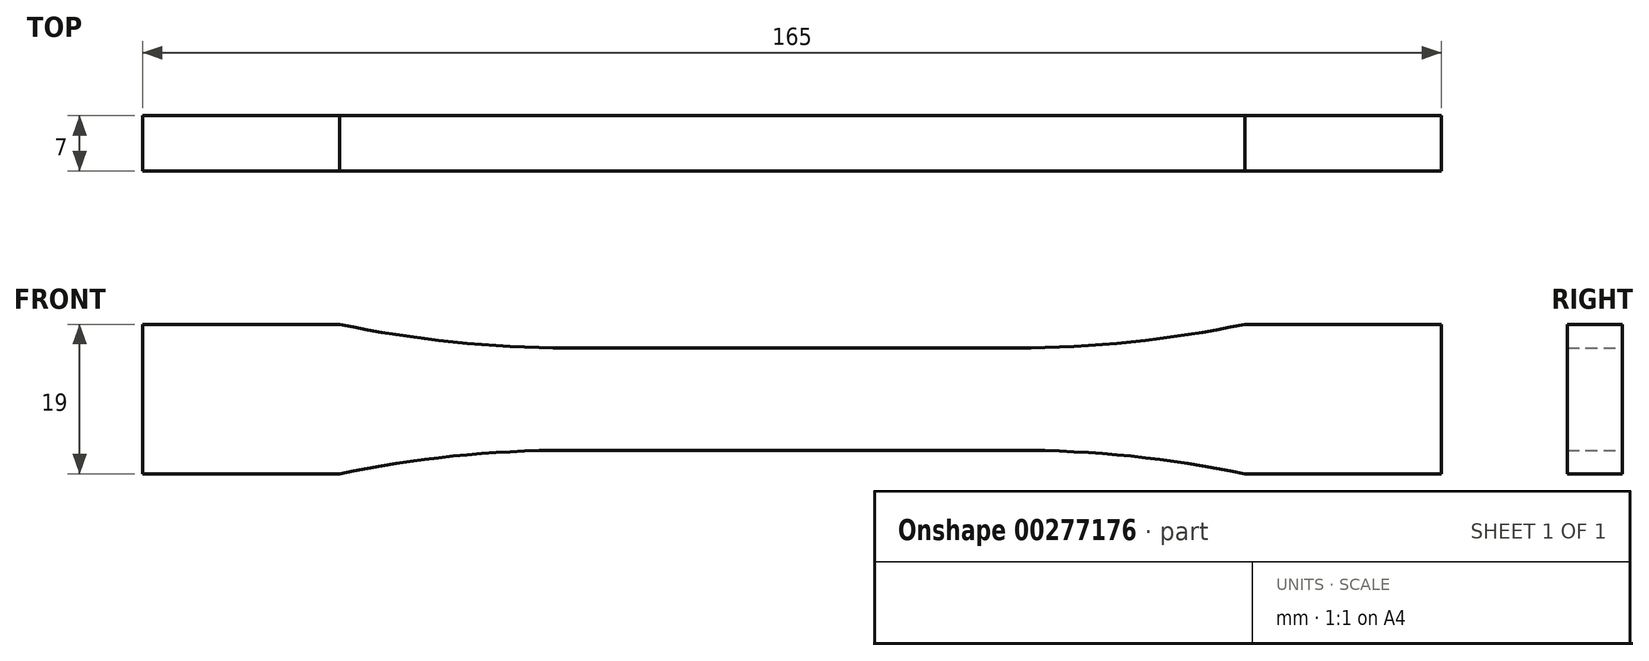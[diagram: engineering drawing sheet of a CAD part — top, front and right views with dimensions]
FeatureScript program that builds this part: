
annotation { "Feature Type Name" : "Feature", "Feature Type Description" : "" }
export const myFeature = defineFeature(function(context is Context, id is Id, definition is map)
    precondition{}
    {
        {
            var Q0;
            Q0=qCreatedBy(makeId("Front.planeOp"),FACE);
            var sketch = newSketch(context, id + "F0", { "sketchPlane" : qUnion([Q0])});
            skLineSegment(sketch, "E0", {"start": v(0, 6.5) * mm, "end": v(28.5, 6.5) * mm});
            skArc(sketch, "E1", {"start": v(28.5, 6.5) * mm, "mid": v(43.08, 7.25) * mm, "end": v(57.5, 9.5) * mm});
            skLineSegment(sketch, "E2", {"start": v(57.5, 9.5) * mm, "end": v(82.5, 9.5) * mm});
            skLineSegment(sketch, "E3", {"start": v(82.5, 9.5) * mm, "end": v(82.5, 0) * mm});
            skLineSegment(sketch, "E4.MirrorCS", {"start": v(0, -6.5) * mm, "end": v(28.5, -6.5) * mm});
            skLineSegment(sketch, "E5.MirrorCS", {"start": v(82.5, -9.5) * mm, "end": v(82.5, 0) * mm});
            skLineSegment(sketch, "E6.MirrorCS", {"start": v(57.5, -9.5) * mm, "end": v(82.5, -9.5) * mm});
            skArc(sketch, "E7.MirrorCS", {"start": v(28.5, -6.5) * mm, "mid": v(43.08, -7.25) * mm, "end": v(57.5, -9.5) * mm});
            skLineSegment(sketch, "E8.MirrorCS", {"start": v(0, 6.5) * mm, "end": v(-28.5, 6.5) * mm});
            skLineSegment(sketch, "E9.MirrorCS", {"start": v(0, -6.5) * mm, "end": v(-28.5, -6.5) * mm});
            skLineSegment(sketch, "E10.MirrorCS", {"start": v(-57.5, -9.5) * mm, "end": v(-82.5, -9.5) * mm});
            skArc(sketch, "E11.MirrorCS", {"start": v(-28.5, 6.5) * mm, "mid": v(-43.08, 7.25) * mm, "end": v(-57.5, 9.5) * mm});
            skLineSegment(sketch, "E12.MirrorCS", {"start": v(-57.5, 9.5) * mm, "end": v(-82.5, 9.5) * mm});
            skLineSegment(sketch, "E13.MirrorCS", {"start": v(-82.5, -9.5) * mm, "end": v(-82.5, 0) * mm});
            skLineSegment(sketch, "E14.MirrorCS", {"start": v(-82.5, 9.5) * mm, "end": v(-82.5, 0) * mm});
            skArc(sketch, "E15.MirrorCS", {"start": v(-28.5, -6.5) * mm, "mid": v(-43.08, -7.25) * mm, "end": v(-57.5, -9.5) * mm});
            skSolve(sketch);
        }
        {
            var Q0;
            Q0=makeQuery(id+"F0.imprint","IMPRINT",FACE,{"disambiguationData":[TD([[makeQuery(id+"F0.imprint","IMPRINT",EDGE,{"derivedFrom":sQuery(id+"F0.wireOp",EDGE,"E1")}),-1.0]])]});
            extrude(context, id + "F1", {"entities" : qUnion([Q0]), "endBound" : BoundingType.SYMMETRIC, "depth" : 7 * mm});
        }
    });
